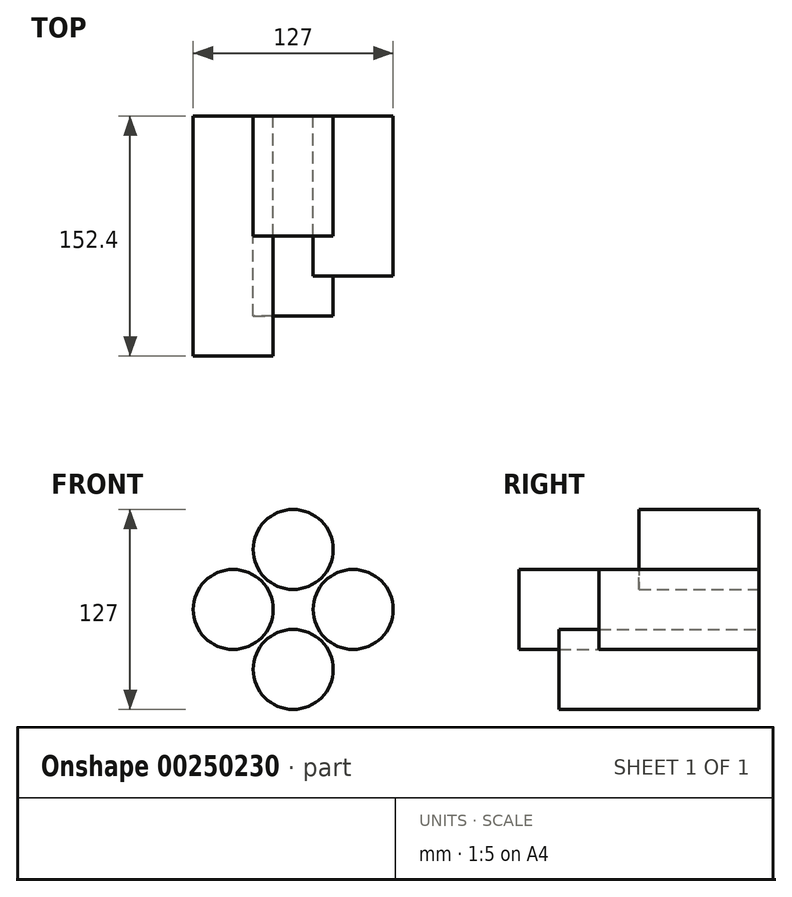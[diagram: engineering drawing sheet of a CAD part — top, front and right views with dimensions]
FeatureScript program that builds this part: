
annotation { "Feature Type Name" : "Feature", "Feature Type Description" : "" }
export const myFeature = defineFeature(function(context is Context, id is Id, definition is map)
    precondition{}
    {
        {
            var Q0;
            Q0=qCreatedBy(makeId("Front.planeOp"),FACE);
            var sketch = newSketch(context, id + "F0", { "sketchPlane" : qUnion([Q0])});
            skCircle(sketch, "E0", {"center": v(0, 0) * mm, "radius": 63.5 * mm});
            skLineSegment(sketch, "E1", {"start": v(0, 0) * mm, "end": v(0, 38.1) * mm});
            skCircle(sketch, "E2", {"center": v(0, 38.1) * mm, "radius": 25.4 * mm});
            skSolve(sketch);
        }
        {
            var Q0;
            {var subQ0=sQuery(id+"F0.wireOp",EDGE,"E2");var subQ2=makeQuery(id+"F0.imprint","IMPRINT",VERTEX,{"derivedFrom":subQ0});Q0=makeQuery(id+"F0.imprint","IMPRINT",FACE,{"disambiguationData":[TD([[makeQuery(id+"F0.imprint","IMPRINT",EDGE,{"disambiguationData":[TD([[subQ2,1.0]])],"derivedFrom":subQ0}),1.0]])]});}
            extrude(context, id + "F1", {"entities" : qUnion([Q0]), "depth" : 76.2 * mm});
        }
        {
            var Q0;
            Q0=sQuery(id+"F0.wireOp",EDGE,"E0");
            extrude(context, id + "F2", {"bodyType" : ToolBodyType.SURFACE, "surfaceEntities" : qUnion([Q0]), "depth" : 50.8 * mm});
        }
        {
            var Q0;
            Q0=qCreatedBy(makeId("Front.planeOp"),FACE);
            var sketch = newSketch(context, id + "F3", { "sketchPlane" : qUnion([Q0])});
            skLineSegment(sketch, "E3", {"start": v(0, 0) * mm, "end": v(0, -38.1) * mm});
            skCircle(sketch, "E4", {"center": v(0, -38.1) * mm, "radius": 25.4 * mm});
            skSolve(sketch);
        }
        {
            var Q0;
            Q0=makeQuery(id+"F3.imprint","IMPRINT",FACE,{"disambiguationData":[TD([[makeQuery(id+"F3.imprint","IMPRINT",EDGE,{"derivedFrom":sQuery(id+"F3.wireOp",EDGE,"E4")}),1.0]])]});
            extrude(context, id + "F4", {"entities" : qUnion([Q0]), "depth" : 127 * mm});
        }
        {
            var Q0;
            Q0=qCreatedBy(makeId("Front.planeOp"),FACE);
            var sketch = newSketch(context, id + "F5", { "sketchPlane" : qUnion([Q0])});
            skLineSegment(sketch, "E5", {"start": v(0, 0) * mm, "end": v(-38.1, 0) * mm});
            skLineSegment(sketch, "E6", {"start": v(0, 0) * mm, "end": v(38.1, 0) * mm});
            skCircle(sketch, "E7", {"center": v(-38.1, 0) * mm, "radius": 25.4 * mm});
            skCircle(sketch, "E8", {"center": v(38.1, 0) * mm, "radius": 25.4 * mm});
            skSolve(sketch);
        }
        {
            var Q0;
            Q0=makeQuery(id+"F5.imprint","IMPRINT",FACE,{"disambiguationData":[TD([[makeQuery(id+"F5.imprint","IMPRINT",EDGE,{"derivedFrom":sQuery(id+"F5.wireOp",EDGE,"E7")}),1.0]])]});
            extrude(context, id + "F6", {"entities" : qUnion([Q0]), "depth" : 152.4 * mm});
        }
        {
            var Q0;
            Q0=makeQuery(id+"F5.imprint","IMPRINT",FACE,{"disambiguationData":[TD([[makeQuery(id+"F5.imprint","IMPRINT",EDGE,{"derivedFrom":sQuery(id+"F5.wireOp",EDGE,"E8")}),1.0]])]});
            extrude(context, id + "F7", {"entities" : qUnion([Q0]), "depth" : 101.6 * mm});
        }
    });
